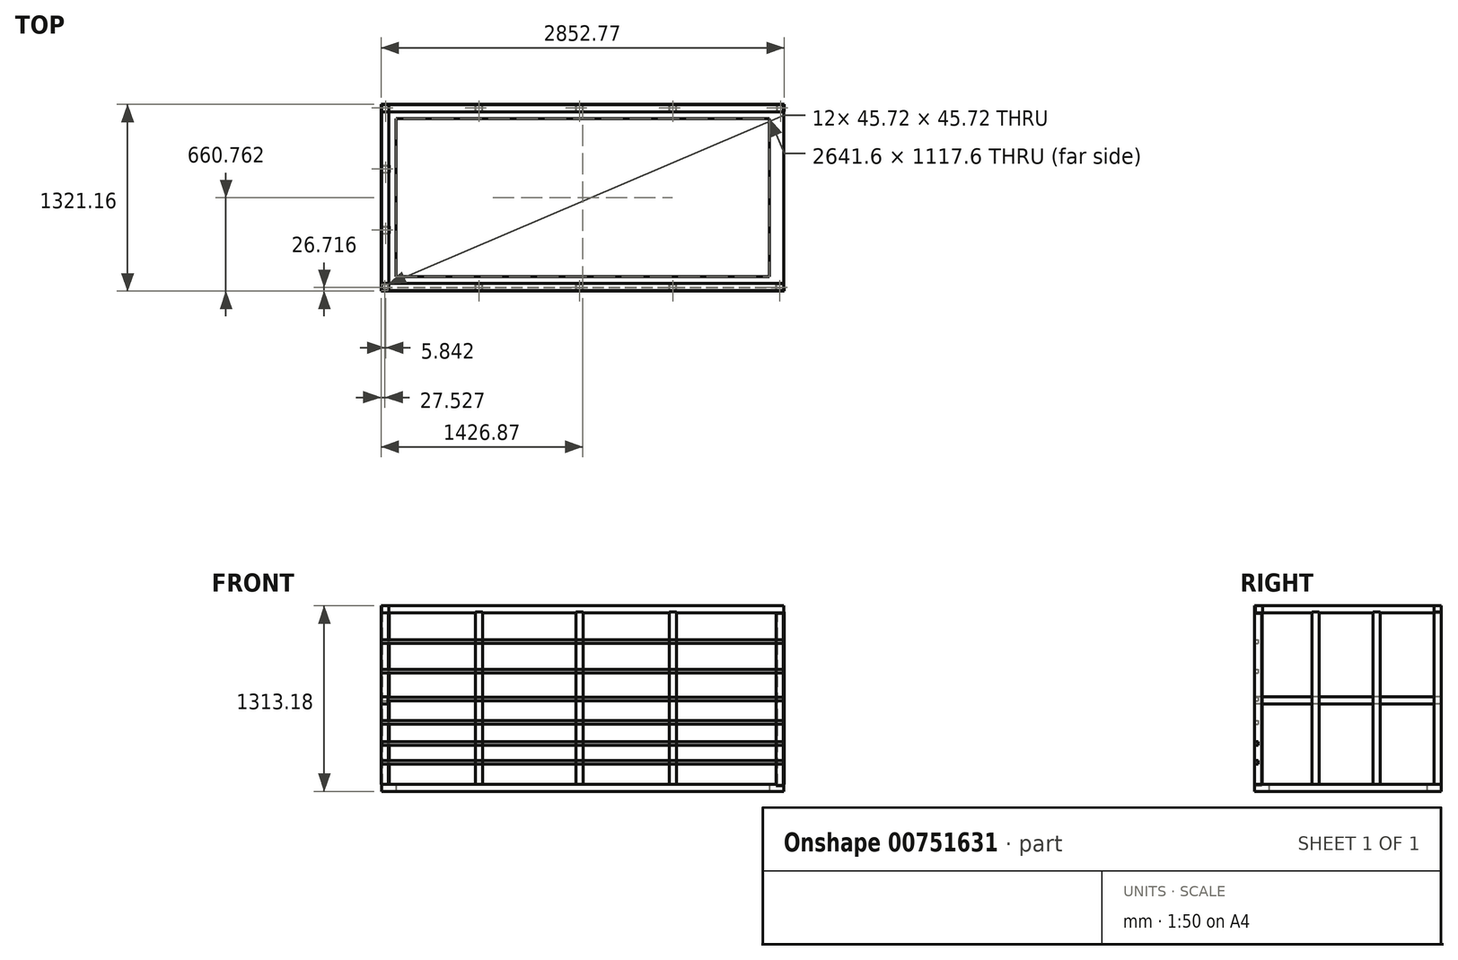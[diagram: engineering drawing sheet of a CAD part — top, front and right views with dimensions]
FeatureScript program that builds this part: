
annotation { "Feature Type Name" : "Feature", "Feature Type Description" : "" }
export const myFeature = defineFeature(function(context is Context, id is Id, definition is map)
    precondition{}
    {
        {
            var Q0;
            Q0=qCreatedBy(makeId("Top.planeOp"),FACE);
            var sketch = newSketch(context, id + "F0", { "sketchPlane" : qUnion([Q0])});
            skLineSegment(sketch, "E0.bottom", {"start": v(-1404.99, 749.36) * mm, "end": v(1439.81, 749.36) * mm});
            skLineSegment(sketch, "E0.top", {"start": v(-1404.99, -571.44) * mm, "end": v(1439.81, -571.44) * mm});
            skLineSegment(sketch, "E0.left", {"start": v(-1404.99, 749.36) * mm, "end": v(-1404.99, -571.44) * mm});
            skLineSegment(sketch, "E0.right", {"start": v(1439.81, 749.36) * mm, "end": v(1439.81, -571.44) * mm});
            skSolve(sketch);
        }
        {
            var Q0;
            Q0=makeQuery(id+"F0.imprint","IMPRINT",FACE,{"disambiguationData":[TD([[makeQuery(id+"F0.imprint","IMPRINT",EDGE,{"derivedFrom":sQuery(id+"F0.wireOp",EDGE,"E0.bottom")}),-1.0]])]});
            extrude(context, id + "F1", {"entities" : qUnion([Q0]), "depth" : 50.8 * mm, "offsetDistance" : 25.4 * mm});
        }
        {
            var Q0;
            Q0=makeQuery(id+"F1.opExtrude","CAP_FACE",FACE,{"disambiguationData":[OSD([sQuery(id+"F0.wireOp",EDGE,"E0.bottom"),sQuery(id+"F0.wireOp",EDGE,"E0.top"),sQuery(id+"F0.wireOp",EDGE,"E0.left"),sQuery(id+"F0.wireOp",EDGE,"E0.right")])],"isStart":false});
            var Q1;
            Q1=makeQuery(id+"F1.opExtrude","CAP_FACE",FACE,{"disambiguationData":[OSD([sQuery(id+"F0.wireOp",EDGE,"E0.bottom"),sQuery(id+"F0.wireOp",EDGE,"E0.top"),sQuery(id+"F0.wireOp",EDGE,"E0.left"),sQuery(id+"F0.wireOp",EDGE,"E0.right")])],"isStart":true});
            shell(context, id + "F2", {"entities" : qUnion([Q0, Q1]), "thickness" : 101.6 * mm});
        }
        {
            var Q0;
            Q0=qCreatedBy(makeId("Front.planeOp"),FACE);
            var sketch = newSketch(context, id + "F3", { "sketchPlane" : qUnion([Q0])});
            skLineSegment(sketch, "E1.bottom", {"start": v(-1515.8, -423.87) * mm, "end": v(-1465, -423.87) * mm});
            skLineSegment(sketch, "E1.top", {"start": v(-1515.8, 795.33) * mm, "end": v(-1465, 795.33) * mm});
            skLineSegment(sketch, "E1.left", {"start": v(-1515.8, -423.87) * mm, "end": v(-1515.8, 795.33) * mm});
            skLineSegment(sketch, "E1.right", {"start": v(-1465, -423.87) * mm, "end": v(-1465, 795.33) * mm});
            skSolve(sketch);
        }
        {
            var Q0;
            Q0 = qSketchRegion(id + "F3", true);
            extrude(context, id + "F4", {"entities" : qUnion([Q0]), "depth" : 50.8 * mm, "offsetDistance" : 25.4 * mm});
        }
        {
            var Q0;
            Q0=makeQuery(id+"F4.opExtrude","SWEPT_FACE",FACE,{"disambiguationData":[OSD([sQuery(id+"F3.wireOp",EDGE,"E1.top")])]});
            var Q1;
            Q1=makeQuery(id+"F4.opExtrude","SWEPT_FACE",FACE,{"disambiguationData":[OSD([sQuery(id+"F3.wireOp",EDGE,"E1.bottom")])]});
            shell(context, id + "F5", {"entities" : qUnion([Q0, Q1]), "thickness" : 2.54 * mm});
        }
        {
            var Q0;
            Q0=makeQuery(id+"F4.opExtrude","SWEPT_BODY",BODY,{"disambiguationData":[OSD([sQuery(id+"F3.wireOp",EDGE,"E1.bottom"),sQuery(id+"F3.wireOp",EDGE,"E1.top"),sQuery(id+"F3.wireOp",EDGE,"E1.left"),sQuery(id+"F3.wireOp",EDGE,"E1.right")])]});
            transform(context, id + "F6", {"entities" : qUnion([Q0]), "transformType" : TransformType.TRANSLATION_3D, "dx" : 114.3 * mm, "dy" : 749.3 * mm, "dz" : 472.44 * mm, "makeCopy" : true});
        }
        {
            var Q0;
            Q0=makeQuery(id+"F4.opExtrude","SWEPT_BODY",BODY,{"disambiguationData":[OSD([sQuery(id+"F3.wireOp",EDGE,"E1.bottom"),sQuery(id+"F3.wireOp",EDGE,"E1.top"),sQuery(id+"F3.wireOp",EDGE,"E1.left"),sQuery(id+"F3.wireOp",EDGE,"E1.right")])]});
            var Q1;
            Q1=makeQuery(id+"F4.opExtrude","CAP_VERTEX",VERTEX,{"disambiguationData":[OSD([sQuery(id+"F3.wireOp",EDGE,"E1.top"),sQuery(id+"F3.wireOp",EDGE,"E1.left")])],"isStart":false});
            var Q2;
            Q2=makeQuery(id+"F4.opExtrude","CAP_VERTEX",VERTEX,{"disambiguationData":[OSD([sQuery(id+"F3.wireOp",EDGE,"E1.top"),sQuery(id+"F3.wireOp",EDGE,"E1.right")])],"isStart":false});
            transform(context, id + "F7", {"entities" : qUnion([Q0]), "transformType" : TransformType.TRANSLATION_ENTITY, "oppositeDirectionEntity" : false, "transformLine" : qUnion([Q1, Q2]), "makeCopy" : false});
        }
        {
            var Q0;
            Q0=makeQuery(id+"F4.opExtrude","SWEPT_BODY",BODY,{"disambiguationData":[OSD([sQuery(id+"F3.wireOp",EDGE,"E1.bottom"),sQuery(id+"F3.wireOp",EDGE,"E1.top"),sQuery(id+"F3.wireOp",EDGE,"E1.left"),sQuery(id+"F3.wireOp",EDGE,"E1.right")])]});
            transform(context, id + "F8", {"entities" : qUnion([Q0]), "transformType" : TransformType.TRANSLATION_3D, "dx" : 76.2 * mm, "dy" : -508 * mm, "dz" : 457.2 * mm, "makeCopy" : false});
        }
        {
            var Q0;
            Q0=makeQuery(id+"F4.opExtrude","SWEPT_BODY",BODY,{"disambiguationData":[OSD([sQuery(id+"F3.wireOp",EDGE,"E1.bottom"),sQuery(id+"F3.wireOp",EDGE,"E1.top"),sQuery(id+"F3.wireOp",EDGE,"E1.left"),sQuery(id+"F3.wireOp",EDGE,"E1.right")])]});
            transform(context, id + "F9", {"entities" : qUnion([Q0]), "transformType" : TransformType.TRANSLATION_3D, "dx" : 2768.6 * mm, "dy" : 0 * mm, "dz" : 0 * mm, "makeCopy" : true});
        }
        {
            var Q0;
            Q0=makeQuery(id+"F6.opPattern","COPY",BODY,{"derivedFrom":makeQuery(id+"F4.opExtrude","SWEPT_BODY",BODY,{"disambiguationData":[OSD([sQuery(id+"F3.wireOp",EDGE,"E1.bottom"),sQuery(id+"F3.wireOp",EDGE,"E1.top"),sQuery(id+"F3.wireOp",EDGE,"E1.left"),sQuery(id+"F3.wireOp",EDGE,"E1.right")])]}),"instanceName":"1"});
            transform(context, id + "F10", {"entities" : qUnion([Q0]), "transformType" : TransformType.TRANSLATION_3D, "dx" : 2794 * mm, "dy" : 0 * mm, "dz" : 0 * mm, "makeCopy" : true});
        }
        {
            var Q0;
            Q0=makeQuery(id+"F6.opPattern","COPY",BODY,{"derivedFrom":makeQuery(id+"F4.opExtrude","SWEPT_BODY",BODY,{"disambiguationData":[OSD([sQuery(id+"F3.wireOp",EDGE,"E1.bottom"),sQuery(id+"F3.wireOp",EDGE,"E1.top"),sQuery(id+"F3.wireOp",EDGE,"E1.left"),sQuery(id+"F3.wireOp",EDGE,"E1.right")])]}),"instanceName":"1"});
            transform(context, id + "F11", {"entities" : qUnion([Q0]), "transformType" : TransformType.TRANSLATION_3D, "dx" : 660.4 * mm, "dy" : 0 * mm, "dz" : 0 * mm, "makeCopy" : true});
        }
        {
            var Q0;
            Q0=makeQuery(id+"F6.opPattern","COPY",BODY,{"derivedFrom":makeQuery(id+"F4.opExtrude","SWEPT_BODY",BODY,{"disambiguationData":[OSD([sQuery(id+"F3.wireOp",EDGE,"E1.bottom"),sQuery(id+"F3.wireOp",EDGE,"E1.top"),sQuery(id+"F3.wireOp",EDGE,"E1.left"),sQuery(id+"F3.wireOp",EDGE,"E1.right")])]}),"instanceName":"1"});
            transform(context, id + "F12", {"entities" : qUnion([Q0]), "transformType" : TransformType.TRANSLATION_3D, "dx" : 2032 * mm, "dy" : 0 * mm, "dz" : 0 * mm, "makeCopy" : true});
        }
        {
            var Q0;
            Q0=makeQuery(id+"F6.opPattern","COPY",BODY,{"derivedFrom":makeQuery(id+"F4.opExtrude","SWEPT_BODY",BODY,{"disambiguationData":[OSD([sQuery(id+"F3.wireOp",EDGE,"E1.bottom"),sQuery(id+"F3.wireOp",EDGE,"E1.top"),sQuery(id+"F3.wireOp",EDGE,"E1.left"),sQuery(id+"F3.wireOp",EDGE,"E1.right")])]}),"instanceName":"1"});
            transform(context, id + "F13", {"entities" : qUnion([Q0]), "transformType" : TransformType.TRANSLATION_3D, "dx" : 1371.6 * mm, "dy" : 0 * mm, "dz" : 0 * mm, "makeCopy" : true});
        }
        {
            var Q0;
            Q0=makeQuery(id+"F6.opPattern","COPY",BODY,{"derivedFrom":makeQuery(id+"F4.opExtrude","SWEPT_BODY",BODY,{"disambiguationData":[OSD([sQuery(id+"F3.wireOp",EDGE,"E1.bottom"),sQuery(id+"F3.wireOp",EDGE,"E1.top"),sQuery(id+"F3.wireOp",EDGE,"E1.left"),sQuery(id+"F3.wireOp",EDGE,"E1.right")])]}),"instanceName":"1"});
            transform(context, id + "F14", {"entities" : qUnion([Q0]), "transformType" : TransformType.TRANSLATION_3D, "dx" : 660.4 * mm, "dy" : -1270 * mm, "dz" : 0 * mm, "makeCopy" : true});
        }
        {
            var Q0;
            Q0=makeQuery(id+"F6.opPattern","COPY",BODY,{"derivedFrom":makeQuery(id+"F4.opExtrude","SWEPT_BODY",BODY,{"disambiguationData":[OSD([sQuery(id+"F3.wireOp",EDGE,"E1.bottom"),sQuery(id+"F3.wireOp",EDGE,"E1.top"),sQuery(id+"F3.wireOp",EDGE,"E1.left"),sQuery(id+"F3.wireOp",EDGE,"E1.right")])]}),"instanceName":"1"});
            transform(context, id + "F15", {"entities" : qUnion([Q0]), "transformType" : TransformType.TRANSLATION_3D, "dx" : 1371.6 * mm, "dy" : -1270 * mm, "dz" : 0 * mm, "makeCopy" : true});
        }
        {
            var Q0;
            Q0=makeQuery(id+"F6.opPattern","COPY",BODY,{"derivedFrom":makeQuery(id+"F4.opExtrude","SWEPT_BODY",BODY,{"disambiguationData":[OSD([sQuery(id+"F3.wireOp",EDGE,"E1.bottom"),sQuery(id+"F3.wireOp",EDGE,"E1.top"),sQuery(id+"F3.wireOp",EDGE,"E1.left"),sQuery(id+"F3.wireOp",EDGE,"E1.right")])]}),"instanceName":"1"});
            transform(context, id + "F16", {"entities" : qUnion([Q0]), "transformType" : TransformType.TRANSLATION_3D, "dx" : 2032 * mm, "dy" : -1270 * mm, "dz" : 0 * mm, "makeCopy" : true});
        }
        {
            var Q0;
            Q0=makeQuery(id+"F6.opPattern","COPY",BODY,{"derivedFrom":makeQuery(id+"F4.opExtrude","SWEPT_BODY",BODY,{"disambiguationData":[OSD([sQuery(id+"F3.wireOp",EDGE,"E1.bottom"),sQuery(id+"F3.wireOp",EDGE,"E1.top"),sQuery(id+"F3.wireOp",EDGE,"E1.left"),sQuery(id+"F3.wireOp",EDGE,"E1.right")])]}),"instanceName":"1"});
            transform(context, id + "F17", {"entities" : qUnion([Q0]), "transformType" : TransformType.TRANSLATION_3D, "dx" : 0 * mm, "dy" : -431.8 * mm, "dz" : 0 * mm, "makeCopy" : true});
        }
        {
            var Q0;
            Q0=makeQuery(id+"F6.opPattern","COPY",BODY,{"derivedFrom":makeQuery(id+"F4.opExtrude","SWEPT_BODY",BODY,{"disambiguationData":[OSD([sQuery(id+"F3.wireOp",EDGE,"E1.bottom"),sQuery(id+"F3.wireOp",EDGE,"E1.top"),sQuery(id+"F3.wireOp",EDGE,"E1.left"),sQuery(id+"F3.wireOp",EDGE,"E1.right")])]}),"instanceName":"1"});
            transform(context, id + "F18", {"entities" : qUnion([Q0]), "transformType" : TransformType.TRANSLATION_3D, "dx" : 0 * mm, "dy" : -863.6 * mm, "dz" : 0 * mm, "makeCopy" : true});
        }
        {
            var Q0;
            Q0=makeQuery(id+"F4.opExtrude","SWEPT_BODY",BODY,{"disambiguationData":[OSD([sQuery(id+"F3.wireOp",EDGE,"E1.bottom"),sQuery(id+"F3.wireOp",EDGE,"E1.top"),sQuery(id+"F3.wireOp",EDGE,"E1.left"),sQuery(id+"F3.wireOp",EDGE,"E1.right")])]});
            transform(context, id + "F19", {"entities" : qUnion([Q0]), "transformType" : TransformType.TRANSLATION_3D, "dx" : -12.7 * mm, "dy" : 0 * mm, "dz" : 17.78 * mm, "makeCopy" : false});
        }
        {
            var Q0;
            Q0=makeQuery(id+"F9.opPattern","COPY",BODY,{"derivedFrom":makeQuery(id+"F4.opExtrude","SWEPT_BODY",BODY,{"disambiguationData":[OSD([sQuery(id+"F3.wireOp",EDGE,"E1.bottom"),sQuery(id+"F3.wireOp",EDGE,"E1.top"),sQuery(id+"F3.wireOp",EDGE,"E1.left"),sQuery(id+"F3.wireOp",EDGE,"E1.right")])]}),"instanceName":"1"});
            transform(context, id + "F20", {"entities" : qUnion([Q0]), "transformType" : TransformType.TRANSLATION_3D, "dx" : 10.16 * mm, "dy" : 0 * mm, "dz" : 7.62 * mm, "makeCopy" : false});
        }
        {
            var Q0;
            Q0=makeQuery(id+"F9.opPattern","COPY",BODY,{"derivedFrom":makeQuery(id+"F4.opExtrude","SWEPT_BODY",BODY,{"disambiguationData":[OSD([sQuery(id+"F3.wireOp",EDGE,"E1.bottom"),sQuery(id+"F3.wireOp",EDGE,"E1.top"),sQuery(id+"F3.wireOp",EDGE,"E1.left"),sQuery(id+"F3.wireOp",EDGE,"E1.right")])]}),"instanceName":"1"});
            transform(context, id + "F21", {"entities" : qUnion([Q0]), "transformType" : TransformType.TRANSLATION_3D, "dx" : -2.54 * mm, "dy" : -12.7 * mm, "dz" : 0 * mm, "makeCopy" : false});
        }
        {
            var Q0;
            Q0=makeQuery(id+"F4.opExtrude","SWEPT_BODY",BODY,{"disambiguationData":[OSD([sQuery(id+"F3.wireOp",EDGE,"E1.bottom"),sQuery(id+"F3.wireOp",EDGE,"E1.top"),sQuery(id+"F3.wireOp",EDGE,"E1.left"),sQuery(id+"F3.wireOp",EDGE,"E1.right")])]});
            transform(context, id + "F22", {"entities" : qUnion([Q0]), "transformType" : TransformType.TRANSLATION_3D, "dx" : -5.84 * mm, "dy" : -11.68 * mm, "dz" : 0 * mm, "makeCopy" : false});
        }
        {
            var Q0;
            Q0=qCreatedBy(makeId("Top.planeOp"),FACE);
            var sketch = newSketch(context, id + "F23", { "sketchPlane" : qUnion([Q0])});
            skLineSegment(sketch, "E2.bottom", {"start": v(1443.14, -775.54) * mm, "end": v(-1401.66, -775.54) * mm});
            skLineSegment(sketch, "E2.top", {"start": v(1443.14, -724.74) * mm, "end": v(-1401.66, -724.74) * mm});
            skLineSegment(sketch, "E2.left", {"start": v(1443.14, -775.54) * mm, "end": v(1443.14, -724.74) * mm});
            skLineSegment(sketch, "E2.right", {"start": v(-1401.66, -775.54) * mm, "end": v(-1401.66, -724.74) * mm});
            skSolve(sketch);
        }
        {
            var Q0;
            Q0 = qSketchRegion(id + "F23", true);
            extrude(context, id + "F24", {"entities" : qUnion([Q0]), "depth" : 50.8 * mm, "offsetDistance" : 25.4 * mm});
        }
        {
            var Q0;
            Q0=makeQuery(id+"F24.opExtrude","SWEPT_BODY",BODY,{"disambiguationData":[OSD([sQuery(id+"F23.wireOp",EDGE,"E2.bottom"),sQuery(id+"F23.wireOp",EDGE,"E2.top"),sQuery(id+"F23.wireOp",EDGE,"E2.left"),sQuery(id+"F23.wireOp",EDGE,"E2.right")])]});
            transform(context, id + "F25", {"entities" : qUnion([Q0]), "transformType" : TransformType.TRANSLATION_3D, "dx" : -2.54 * mm, "dy" : 208.28 * mm, "dz" : 1262.38 * mm, "makeCopy" : false});
        }
        {
            var Q0;
            Q0=makeQuery(id+"F24.opExtrude","SWEPT_BODY",BODY,{"disambiguationData":[OSD([sQuery(id+"F23.wireOp",EDGE,"E2.bottom"),sQuery(id+"F23.wireOp",EDGE,"E2.top"),sQuery(id+"F23.wireOp",EDGE,"E2.left"),sQuery(id+"F23.wireOp",EDGE,"E2.right")])]});
            transform(context, id + "F26", {"entities" : qUnion([Q0]), "transformType" : TransformType.TRANSLATION_3D, "dx" : -2.54 * mm, "dy" : 1264.92 * mm, "dz" : 0 * mm, "makeCopy" : true});
        }
        {
            var Q0;
            Q0=qCreatedBy(makeId("Top.planeOp"),FACE);
            var sketch = newSketch(context, id + "F27", { "sketchPlane" : qUnion([Q0])});
            skLineSegment(sketch, "E3.bottom", {"start": v(-1483.12, 754.08) * mm, "end": v(-1533.92, 754.08) * mm});
            skLineSegment(sketch, "E3.top", {"start": v(-1483.12, -566.72) * mm, "end": v(-1533.92, -566.72) * mm});
            skLineSegment(sketch, "E3.left", {"start": v(-1483.12, 754.08) * mm, "end": v(-1483.12, -566.72) * mm});
            skLineSegment(sketch, "E3.right", {"start": v(-1533.92, 754.08) * mm, "end": v(-1533.92, -566.72) * mm});
            skSolve(sketch);
        }
        {
            var Q0;
            Q0 = qSketchRegion(id + "F27", true);
            extrude(context, id + "F28", {"entities" : qUnion([Q0]), "depth" : 50.8 * mm, "offsetDistance" : 25.4 * mm});
        }
        {
            var Q0;
            Q0=makeQuery(id+"F28.opExtrude","SWEPT_BODY",BODY,{"disambiguationData":[OSD([sQuery(id+"F27.wireOp",EDGE,"E3.bottom"),sQuery(id+"F27.wireOp",EDGE,"E3.top"),sQuery(id+"F27.wireOp",EDGE,"E3.left"),sQuery(id+"F27.wireOp",EDGE,"E3.right")])]});
            transform(context, id + "F29", {"entities" : qUnion([Q0]), "transformType" : TransformType.TRANSLATION_3D, "dx" : 129.54 * mm, "dy" : -5.08 * mm, "dz" : 1262.38 * mm, "makeCopy" : false});
        }
        {
            var Q0;
            Q0=makeQuery(id+"F28.opExtrude","SWEPT_BODY",BODY,{"disambiguationData":[OSD([sQuery(id+"F27.wireOp",EDGE,"E3.bottom"),sQuery(id+"F27.wireOp",EDGE,"E3.top"),sQuery(id+"F27.wireOp",EDGE,"E3.left"),sQuery(id+"F27.wireOp",EDGE,"E3.right")])]});
            transform(context, id + "F30", {"entities" : qUnion([Q0]), "transformType" : TransformType.TRANSLATION_3D, "dx" : -5.08 * mm, "dy" : 0 * mm, "dz" : -642.62 * mm, "makeCopy" : true});
        }
        {
            var Q0;
            Q0=qCreatedBy(makeId("Front.planeOp"),FACE);
            var sketch = newSketch(context, id + "F31", { "sketchPlane" : qUnion([Q0])});
            skLineSegment(sketch, "E4.bottom", {"start": v(-1415.4, -211.2) * mm, "end": v(1429.4, -211.2) * mm});
            skLineSegment(sketch, "E4.top", {"start": v(-1415.4, -236.6) * mm, "end": v(1429.4, -236.6) * mm});
            skLineSegment(sketch, "E4.left", {"start": v(-1415.4, -211.2) * mm, "end": v(-1415.4, -236.6) * mm});
            skLineSegment(sketch, "E4.right", {"start": v(1429.4, -211.2) * mm, "end": v(1429.4, -236.6) * mm});
            skSolve(sketch);
        }
        {
            var Q0;
            Q0 = qSketchRegion(id + "F31", true);
            extrude(context, id + "F32", {"entities" : qUnion([Q0]), "depth" : 25.4 * mm, "offsetDistance" : 25.4 * mm});
        }
        {
            var Q0;
            Q0=makeQuery(id+"F32.opExtrude","SWEPT_BODY",BODY,{"disambiguationData":[OSD([sQuery(id+"F31.wireOp",EDGE,"E4.bottom"),sQuery(id+"F31.wireOp",EDGE,"E4.top"),sQuery(id+"F31.wireOp",EDGE,"E4.left"),sQuery(id+"F31.wireOp",EDGE,"E4.right")])]});
            transform(context, id + "F33", {"entities" : qUnion([Q0]), "transformType" : TransformType.TRANSLATION_3D, "dx" : 10.16 * mm, "dy" : -546.1 * mm, "dz" : 429.26 * mm, "makeCopy" : false});
        }
        {
            var Q0;
            Q0=makeQuery(id+"F32.opExtrude","SWEPT_BODY",BODY,{"disambiguationData":[OSD([sQuery(id+"F31.wireOp",EDGE,"E4.bottom"),sQuery(id+"F31.wireOp",EDGE,"E4.top"),sQuery(id+"F31.wireOp",EDGE,"E4.left"),sQuery(id+"F31.wireOp",EDGE,"E4.right")])]});
            transform(context, id + "F34", {"entities" : qUnion([Q0]), "transformType" : TransformType.TRANSLATION_3D, "dx" : 2.54 * mm, "dy" : 0 * mm, "dz" : 132.08 * mm, "makeCopy" : true});
        }
        {
            var Q0;
            Q0=makeQuery(id+"F32.opExtrude","SWEPT_BODY",BODY,{"disambiguationData":[OSD([sQuery(id+"F31.wireOp",EDGE,"E4.bottom"),sQuery(id+"F31.wireOp",EDGE,"E4.top"),sQuery(id+"F31.wireOp",EDGE,"E4.left"),sQuery(id+"F31.wireOp",EDGE,"E4.right")])]});
            transform(context, id + "F35", {"entities" : qUnion([Q0]), "transformType" : TransformType.TRANSLATION_3D, "dx" : -2.54 * mm, "dy" : 0 * mm, "dz" : 281.94 * mm, "makeCopy" : true});
        }
        {
            var Q0;
            Q0=makeQuery(id+"F32.opExtrude","SWEPT_BODY",BODY,{"disambiguationData":[OSD([sQuery(id+"F31.wireOp",EDGE,"E4.bottom"),sQuery(id+"F31.wireOp",EDGE,"E4.top"),sQuery(id+"F31.wireOp",EDGE,"E4.left"),sQuery(id+"F31.wireOp",EDGE,"E4.right")])]});
            transform(context, id + "F36", {"entities" : qUnion([Q0]), "transformType" : TransformType.TRANSLATION_3D, "dx" : -2.54 * mm, "dy" : 0 * mm, "dz" : 447.04 * mm, "makeCopy" : true});
        }
        {
            var Q0;
            Q0=makeQuery(id+"F32.opExtrude","SWEPT_BODY",BODY,{"disambiguationData":[OSD([sQuery(id+"F31.wireOp",EDGE,"E4.bottom"),sQuery(id+"F31.wireOp",EDGE,"E4.top"),sQuery(id+"F31.wireOp",EDGE,"E4.left"),sQuery(id+"F31.wireOp",EDGE,"E4.right")])]});
            transform(context, id + "F37", {"entities" : qUnion([Q0]), "transformType" : TransformType.TRANSLATION_3D, "dx" : -2.54 * mm, "dy" : 0 * mm, "dz" : 645.16 * mm, "makeCopy" : true});
        }
        {
            var Q0;
            Q0=makeQuery(id+"F32.opExtrude","SWEPT_BODY",BODY,{"disambiguationData":[OSD([sQuery(id+"F31.wireOp",EDGE,"E4.bottom"),sQuery(id+"F31.wireOp",EDGE,"E4.top"),sQuery(id+"F31.wireOp",EDGE,"E4.left"),sQuery(id+"F31.wireOp",EDGE,"E4.right")])]});
            transform(context, id + "F38", {"entities" : qUnion([Q0]), "transformType" : TransformType.TRANSLATION_3D, "dx" : -2.54 * mm, "dy" : 0 * mm, "dz" : 853.44 * mm, "makeCopy" : true});
        }
    });
